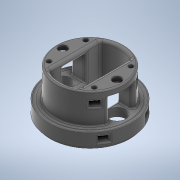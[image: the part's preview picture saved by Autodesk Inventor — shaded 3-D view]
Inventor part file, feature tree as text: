
AUTODESK INVENTOR PART (.ipt)
format: ipt  version: 2020 (Build 240168000, 168)  size: 812,032 bytes
history: native  units: in
note: dims shown in document units (in); Inventor stores cm internally (conversion verified against a paired STEP export)
features: sketch x12, extrude x7, hole x3, revolve x2, plane x2, fillet x2
ambient origin geometry x8: Origin, YZ Plane, XZ Plane, XY Plane, X Axis, Y Axis, Z Axis, Center Point
bodies: Solid1 (feature_tree)
feature tree (28):
  revolve  "Revolution1"  [1 undecoded]
  hole  "Hole1"  [1 undecoded]
  extrude  "Extrusion1"  Depth=2.4in
  plane  "Work Plane1"
  extrude  "Extrusion3"  Depth=1.0in
  extrude  "Extrusion4"  Depth=0.125in
  extrude  "Extrusion5"  Depth=0.3125in TaperAngle=0.0deg
  plane  "Work Plane2"
  extrude  "Extrusion6"  Depth=1.875in
  hole  "Hole2"  [1 undecoded]
  revolve  "Revolution2"  [1 undecoded]
  extrude  "Extrusion8"  Depth=2.25in
  hole  "Hole3"  [1 undecoded]
  extrude  "Extrusion9"  Depth=0.0625in TaperAngle=0.0deg
  fillet  "Fillet7"  [1 undecoded]
  fillet  "Fillet8"  Radius=0.375in
  sketch  "Sketch1"  dims[d3=1.5in d4=0.125in]
  sketch  "Sketch2"  dims[d5=1.75in d6=0.1in]
  sketch  "Sketch3"  dims[d8=90.0deg d9=2.4in]
  sketch  "Sketch5"  dims[d10=1.5in]
  sketch  "Sketch6"  dims[d11=0.2031in d12=0.75in d13=0.3125in d14=0.875in d15=0.5635in d16=0.5in d17=0.0in d18=1.0in]
  sketch  "Sketch7"  dims[d19=0.125in d20=2.4in]
  sketch  "Sketch8"  dims[d21=2.0in d22=0.3125in d23=0.0in]
  sketch  "Sketch9"  dims[d28=0.55in d29=1.875in]
  sketch  "Sketch10"  dims[d30=-0.25in d31=2.4in]
  sketch  "Sketch13"  dims[d32=1.0in d33=0.375in d34=0.0in]
  sketch  "Sketch14"  dims[d35=1.375in d36=2.25in]
  sketch  "Sketch15"  dims[d37=0.625in d38=0.0in d39=0.75in d40=0.75in d41=0.0in d42=-0.375in d43=0.375in d44=0.25in d45=0.0in d46=0.375in d47=0.75in d48=0.5in d49=0.188in d50=0.5635in d51=1.0in d52=0.8108in d56=0.125in d57=1.75in d58=0.02in d59=90.0deg d67=1.781in d68=0.0in d71=2.0in d72=1.625in d73=0.2031in d74=0.75in d75=0.375in d76=0.25in d77=0.5635in d78=0.625in d79=0.0in d80=0.375in d81=0.25in d82=0.0in d83=0.125in d84=0.0625in]
note: 6 required parameter values undecoded (feature->parameter linkage not recoverable at this tier; creation-order binding heuristic only, values carry confidence <= 0.55)